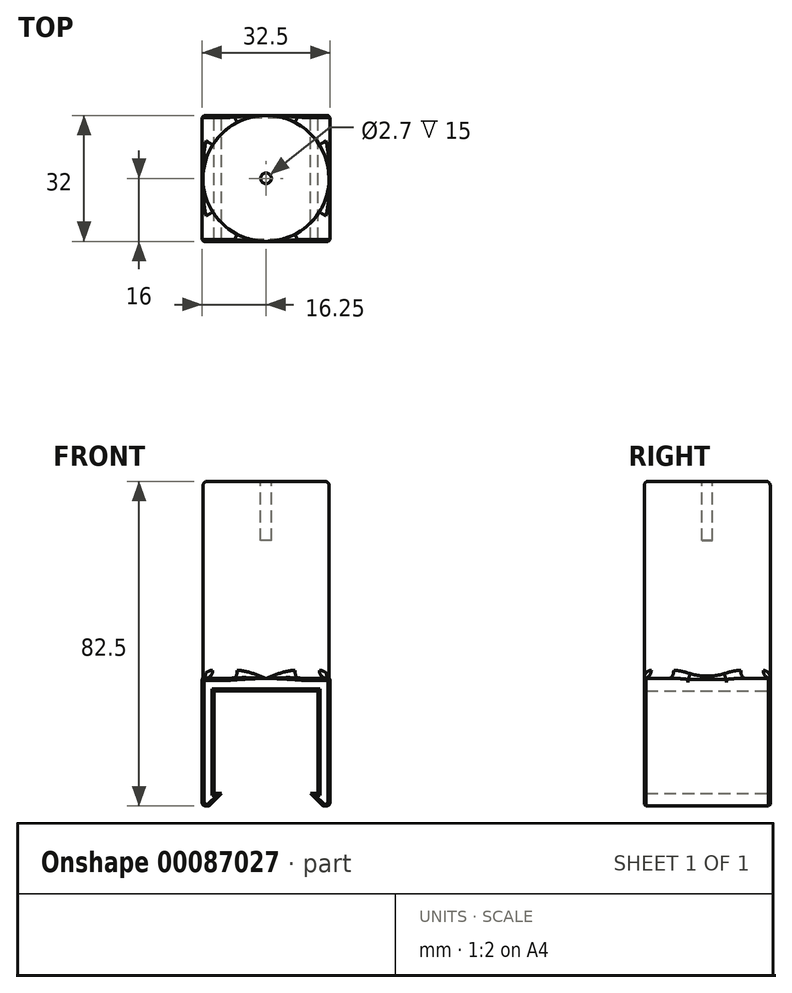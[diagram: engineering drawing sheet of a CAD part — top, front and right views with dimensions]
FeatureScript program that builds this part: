
annotation { "Feature Type Name" : "Feature", "Feature Type Description" : "" }
export const myFeature = defineFeature(function(context is Context, id is Id, definition is map)
    precondition{}
    {
        {
            var Q0;
            Q0=qCreatedBy(makeId("Front.planeOp"),FACE);
            var sketch = newSketch(context, id + "F0", { "sketchPlane" : qUnion([Q0])});
            skLineSegment(sketch, "E0.top", {"start": v(13.25, 13) * mm, "end": v(-13.25, 13) * mm, "construction": true});
            skLineSegment(sketch, "E0.left", {"start": v(13.25, -13) * mm, "end": v(13.25, 13) * mm, "construction": true});
            skLineSegment(sketch, "E0.right", {"start": v(-13.25, -13) * mm, "end": v(-13.25, 13) * mm, "construction": true});
            skPoint(sketch, "E0.middle", {"position": v(0, 0) * mm});
            skLineSegment(sketch, "E1", {"start": v(-13.25, -13) * mm, "end": v(-13.25, 13) * mm});
            skLineSegment(sketch, "E2", {"start": v(13.25, 13) * mm, "end": v(13.25, -13) * mm});
            skLineSegment(sketch, "E3", {"start": v(11.25, -13) * mm, "end": v(14.5, -16.25) * mm});
            skLineSegment(sketch, "E4", {"start": v(14.5, -16.25) * mm, "end": v(16.25, -16.25) * mm});
            skLineSegment(sketch, "E5", {"start": v(16.25, -16.25) * mm, "end": v(16.25, 16.25) * mm});
            skLineSegment(sketch, "E6", {"start": v(16.25, 16.25) * mm, "end": v(-16.25, 16.25) * mm});
            skLineSegment(sketch, "E7", {"start": v(-16.25, 16.25) * mm, "end": v(-16.25, -16.25) * mm});
            skLineSegment(sketch, "E8", {"start": v(-16.25, -16.25) * mm, "end": v(-14.5, -16.25) * mm});
            skLineSegment(sketch, "E9", {"start": v(-14.5, -16.25) * mm, "end": v(-11.25, -13) * mm});
            skLineSegment(sketch, "E10", {"start": v(-11.25, -13) * mm, "end": v(-13.25, -13) * mm});
            skLineSegment(sketch, "E11", {"start": v(-13.25, 13) * mm, "end": v(13.25, 13) * mm});
            skLineSegment(sketch, "E12", {"start": v(11.25, -13) * mm, "end": v(13.25, -13) * mm});
            skSolve(sketch);
        }
        {
            var Q0;
            Q0 = qSketchRegion(id + "F0", true);
            extrude(context, id + "F1", {"entities" : qUnion([Q0]), "endBound" : BoundingType.SYMMETRIC, "depth" : 32 * mm});
        }
        {
            var Q0;
            Q0=makeQuery(id+"F1.opExtrude","SWEPT_FACE",FACE,{"disambiguationData":[OSD([sQuery(id+"F0.wireOp",EDGE,"E6")])]});
            var sketch = newSketch(context, id + "F2", { "sketchPlane" : qUnion([Q0])});
            skCircle(sketch, "E13", {"center": v(0, 0) * mm, "radius": 16 * mm});
            skSolve(sketch);
        }
        {
            var Q0;
            Q0 = qSketchRegion(id + "F2", true);
            extrude(context, id + "F3", {"entities" : qUnion([Q0]), "operationType" : NewBodyOperationType.ADD, "offsetDistance" : 25 * mm, "depth" : 50 * mm});
        }
        {
            var Q0;
            Q0=makeQuery(id+"F3.opExtrude","CAP_FACE",FACE,{"disambiguationData":[OSD([sQuery(id+"F2.wireOp",EDGE,"E13")])],"isStart":false});
            var sketch = newSketch(context, id + "F4", { "sketchPlane" : qUnion([Q0])});
            skCircle(sketch, "E14", {"center": v(0, 0) * mm, "radius": 1.35 * mm});
            skSolve(sketch);
        }
        {
            var Q0;
            Q0 = qSketchRegion(id + "F4", true);
            extrude(context, id + "F5", {"entities" : qUnion([Q0]), "operationType" : NewBodyOperationType.REMOVE, "oppositeDirection" : true, "depth" : 15 * mm});
        }
        {
            var Q0;
            Q0=makeQuery(id+"F1.opExtrude","SWEPT_EDGE",EDGE,{"disambiguationData":[OSD([sQuery(id+"F0.wireOp",EDGE,"E7"),sQuery(id+"F0.wireOp",EDGE,"E8")])]});
            var Q1;
            Q1=makeQuery(id+"F1.opExtrude","SWEPT_EDGE",EDGE,{"disambiguationData":[OSD([sQuery(id+"F0.wireOp",EDGE,"E8"),sQuery(id+"F0.wireOp",EDGE,"E9")])]});
            var Q2;
            Q2=makeQuery(id+"F1.opExtrude","SWEPT_EDGE",EDGE,{"disambiguationData":[OSD([sQuery(id+"F0.wireOp",EDGE,"E3"),sQuery(id+"F0.wireOp",EDGE,"E4")])]});
            var Q3;
            Q3=makeQuery(id+"F1.opExtrude","SWEPT_EDGE",EDGE,{"disambiguationData":[OSD([sQuery(id+"F0.wireOp",EDGE,"E4"),sQuery(id+"F0.wireOp",EDGE,"E5")])]});
            var Q4;
            {var subQ0=sQuery(id+"F0.wireOp",EDGE,"E6");var subQ1=sQuery(id+"F0.wireOp",EDGE,"E5");Q4=makeQuery(id+"F3.boolean.opBoolean","SPLIT",EDGE,{"disambiguationData":[TD([makeQuery(id+"F1.opExtrude","CAP_FACE",FACE,{"disambiguationData":[OSD([sQuery(id+"F0.wireOp",EDGE,"E1"),sQuery(id+"F0.wireOp",EDGE,"E2"),sQuery(id+"F0.wireOp",EDGE,"E3"),sQuery(id+"F0.wireOp",EDGE,"E4"),subQ1,subQ0,sQuery(id+"F0.wireOp",EDGE,"E7"),sQuery(id+"F0.wireOp",EDGE,"E8"),sQuery(id+"F0.wireOp",EDGE,"E9"),sQuery(id+"F0.wireOp",EDGE,"E10"),sQuery(id+"F0.wireOp",EDGE,"E11"),sQuery(id+"F0.wireOp",EDGE,"E12")])],"isStart":false})])],"derivedFrom":makeQuery(id+"F1.opExtrude","SWEPT_EDGE",EDGE,{"disambiguationData":[OSD([subQ1,subQ0])]})});}
            var Q5;
            {var subQ0=sQuery(id+"F0.wireOp",EDGE,"E7");var subQ1=sQuery(id+"F0.wireOp",EDGE,"E6");Q5=makeQuery(id+"F3.boolean.opBoolean","SPLIT",EDGE,{"disambiguationData":[TD([makeQuery(id+"F1.opExtrude","CAP_FACE",FACE,{"disambiguationData":[OSD([sQuery(id+"F0.wireOp",EDGE,"E1"),sQuery(id+"F0.wireOp",EDGE,"E2"),sQuery(id+"F0.wireOp",EDGE,"E3"),sQuery(id+"F0.wireOp",EDGE,"E4"),sQuery(id+"F0.wireOp",EDGE,"E5"),subQ1,subQ0,sQuery(id+"F0.wireOp",EDGE,"E8"),sQuery(id+"F0.wireOp",EDGE,"E9"),sQuery(id+"F0.wireOp",EDGE,"E10"),sQuery(id+"F0.wireOp",EDGE,"E11"),sQuery(id+"F0.wireOp",EDGE,"E12")])],"isStart":false})])],"derivedFrom":makeQuery(id+"F1.opExtrude","SWEPT_EDGE",EDGE,{"disambiguationData":[OSD([subQ1,subQ0])]})});}
            var Q6;
            Q6=makeQuery(id+"F3.opExtrude","CAP_EDGE",EDGE,{"disambiguationData":[OSD([sQuery(id+"F2.wireOp",EDGE,"E13")])],"isStart":false});
            fillet(context, id + "F6", {"entities" : qUnion([Q0, Q1, Q2, Q3, Q4, Q5, Q6]), "radius" : 1 * mm, "tangentPropagation" : true, "allowEdgeOverflow" : false});
        }
        {
            var Q0;
            {var subQ0=sQuery(id+"F2.wireOp",EDGE,"E13");var subQ1=makeQuery(id+"F3.opExtrude","SWEPT_FACE",FACE,{"disambiguationData":[OSD([subQ0])]});var subQ2=sQuery(id+"F0.wireOp",EDGE,"E6");var subQ3=sQuery(id+"F0.wireOp",EDGE,"E5");var subQ4=makeQuery(id+"F1.opExtrude","SWEPT_FACE",FACE,{"disambiguationData":[OSD([subQ2])]});Q0=makeQuery(id+"F3.boolean.opBoolean","SPLIT",EDGE,{"disambiguationData":[topologyDisambiguationEdgeConnected([subQ4,subQ1]),TD([makeQuery(id+"F1.opExtrude","CAP_FACE",FACE,{"disambiguationData":[OSD([sQuery(id+"F0.wireOp",EDGE,"E1"),sQuery(id+"F0.wireOp",EDGE,"E2"),sQuery(id+"F0.wireOp",EDGE,"E3"),sQuery(id+"F0.wireOp",EDGE,"E4"),subQ3,subQ2,sQuery(id+"F0.wireOp",EDGE,"E7"),sQuery(id+"F0.wireOp",EDGE,"E8"),sQuery(id+"F0.wireOp",EDGE,"E9"),sQuery(id+"F0.wireOp",EDGE,"E10"),sQuery(id+"F0.wireOp",EDGE,"E11"),sQuery(id+"F0.wireOp",EDGE,"E12")])],"isStart":true}),makeQuery(id+"F1.opExtrude","SWEPT_FACE",FACE,{"disambiguationData":[OSD([subQ3])]}),subQ4,subQ1,makeQuery(id+"F3.opExtrude","CAP_FACE",FACE,{"disambiguationData":[OSD([subQ0])],"isStart":true})])],"derivedFrom":makeQuery(id+"F3.opExtrude","CAP_EDGE",EDGE,{"disambiguationData":[OSD([subQ0])],"isStart":true})});}
            var Q1;
            {var subQ0=sQuery(id+"F2.wireOp",EDGE,"E13");var subQ1=makeQuery(id+"F3.opExtrude","SWEPT_FACE",FACE,{"disambiguationData":[OSD([subQ0])]});var subQ2=sQuery(id+"F0.wireOp",EDGE,"E7");var subQ3=sQuery(id+"F0.wireOp",EDGE,"E6");var subQ4=makeQuery(id+"F1.opExtrude","SWEPT_FACE",FACE,{"disambiguationData":[OSD([subQ3])]});Q1=makeQuery(id+"F3.boolean.opBoolean","SPLIT",EDGE,{"disambiguationData":[topologyDisambiguationEdgeConnected([subQ4,subQ1]),TD([makeQuery(id+"F1.opExtrude","CAP_FACE",FACE,{"disambiguationData":[OSD([sQuery(id+"F0.wireOp",EDGE,"E1"),sQuery(id+"F0.wireOp",EDGE,"E2"),sQuery(id+"F0.wireOp",EDGE,"E3"),sQuery(id+"F0.wireOp",EDGE,"E4"),sQuery(id+"F0.wireOp",EDGE,"E5"),subQ3,subQ2,sQuery(id+"F0.wireOp",EDGE,"E8"),sQuery(id+"F0.wireOp",EDGE,"E9"),sQuery(id+"F0.wireOp",EDGE,"E10"),sQuery(id+"F0.wireOp",EDGE,"E11"),sQuery(id+"F0.wireOp",EDGE,"E12")])],"isStart":true}),subQ4,makeQuery(id+"F1.opExtrude","SWEPT_FACE",FACE,{"disambiguationData":[OSD([subQ2])]}),subQ1,makeQuery(id+"F3.opExtrude","CAP_FACE",FACE,{"disambiguationData":[OSD([subQ0])],"isStart":true})])],"derivedFrom":makeQuery(id+"F3.opExtrude","CAP_EDGE",EDGE,{"disambiguationData":[OSD([subQ0])],"isStart":true})});}
            var Q2;
            {var subQ0=sQuery(id+"F2.wireOp",EDGE,"E13");var subQ1=makeQuery(id+"F3.opExtrude","SWEPT_FACE",FACE,{"disambiguationData":[OSD([subQ0])]});var subQ2=sQuery(id+"F0.wireOp",EDGE,"E7");var subQ3=sQuery(id+"F0.wireOp",EDGE,"E6");var subQ4=makeQuery(id+"F1.opExtrude","SWEPT_FACE",FACE,{"disambiguationData":[OSD([subQ3])]});Q2=makeQuery(id+"F3.boolean.opBoolean","SPLIT",EDGE,{"disambiguationData":[topologyDisambiguationEdgeConnected([subQ4,subQ1]),TD([makeQuery(id+"F1.opExtrude","CAP_FACE",FACE,{"disambiguationData":[OSD([sQuery(id+"F0.wireOp",EDGE,"E1"),sQuery(id+"F0.wireOp",EDGE,"E2"),sQuery(id+"F0.wireOp",EDGE,"E3"),sQuery(id+"F0.wireOp",EDGE,"E4"),sQuery(id+"F0.wireOp",EDGE,"E5"),subQ3,subQ2,sQuery(id+"F0.wireOp",EDGE,"E8"),sQuery(id+"F0.wireOp",EDGE,"E9"),sQuery(id+"F0.wireOp",EDGE,"E10"),sQuery(id+"F0.wireOp",EDGE,"E11"),sQuery(id+"F0.wireOp",EDGE,"E12")])],"isStart":false}),subQ4,makeQuery(id+"F1.opExtrude","SWEPT_FACE",FACE,{"disambiguationData":[OSD([subQ2])]}),subQ1,makeQuery(id+"F3.opExtrude","CAP_FACE",FACE,{"disambiguationData":[OSD([subQ0])],"isStart":true})])],"derivedFrom":makeQuery(id+"F3.opExtrude","CAP_EDGE",EDGE,{"disambiguationData":[OSD([subQ0])],"isStart":true})});}
            var Q3;
            {var subQ0=sQuery(id+"F2.wireOp",EDGE,"E13");var subQ1=makeQuery(id+"F3.opExtrude","SWEPT_FACE",FACE,{"disambiguationData":[OSD([subQ0])]});var subQ2=sQuery(id+"F0.wireOp",EDGE,"E5");var subQ3=sQuery(id+"F0.wireOp",EDGE,"E6");var subQ4=makeQuery(id+"F1.opExtrude","SWEPT_FACE",FACE,{"disambiguationData":[OSD([subQ3])]});Q3=makeQuery(id+"F3.boolean.opBoolean","SPLIT",EDGE,{"disambiguationData":[topologyDisambiguationEdgeConnected([subQ4,subQ1]),TD([makeQuery(id+"F1.opExtrude","CAP_FACE",FACE,{"disambiguationData":[OSD([sQuery(id+"F0.wireOp",EDGE,"E1"),sQuery(id+"F0.wireOp",EDGE,"E2"),sQuery(id+"F0.wireOp",EDGE,"E3"),sQuery(id+"F0.wireOp",EDGE,"E4"),subQ2,subQ3,sQuery(id+"F0.wireOp",EDGE,"E7"),sQuery(id+"F0.wireOp",EDGE,"E8"),sQuery(id+"F0.wireOp",EDGE,"E9"),sQuery(id+"F0.wireOp",EDGE,"E10"),sQuery(id+"F0.wireOp",EDGE,"E11"),sQuery(id+"F0.wireOp",EDGE,"E12")])],"isStart":false}),makeQuery(id+"F1.opExtrude","SWEPT_FACE",FACE,{"disambiguationData":[OSD([subQ2])]}),subQ4,subQ1,makeQuery(id+"F3.opExtrude","CAP_FACE",FACE,{"disambiguationData":[OSD([subQ0])],"isStart":true})])],"derivedFrom":makeQuery(id+"F3.opExtrude","CAP_EDGE",EDGE,{"disambiguationData":[OSD([subQ0])],"isStart":true})});}
            fillet(context, id + "F7", {"entities" : qUnion([Q0, Q1, Q2, Q3]), "radius" : 2 * mm, "tangentPropagation" : true, "defaultsChanged" : false, "vertexSettings" : [], "allowEdgeOverflow" : false});
        }
        {
            var Q0;
            Q0=makeQuery(id+"F1.opExtrude","CAP_EDGE",EDGE,{"disambiguationData":[OSD([sQuery(id+"F0.wireOp",EDGE,"E5")])],"isStart":false});
            var Q1;
            Q1=makeQuery(id+"F1.opExtrude","CAP_EDGE",EDGE,{"disambiguationData":[OSD([sQuery(id+"F0.wireOp",EDGE,"E7")])],"isStart":false});
            var Q2;
            Q2=makeQuery(id+"F1.opExtrude","CAP_EDGE",EDGE,{"disambiguationData":[OSD([sQuery(id+"F0.wireOp",EDGE,"E1")])],"isStart":false});
            var Q3;
            Q3=makeQuery(id+"F1.opExtrude","CAP_EDGE",EDGE,{"disambiguationData":[OSD([sQuery(id+"F0.wireOp",EDGE,"E11")])],"isStart":false});
            var Q4;
            Q4=makeQuery(id+"F1.opExtrude","CAP_EDGE",EDGE,{"disambiguationData":[OSD([sQuery(id+"F0.wireOp",EDGE,"E2")])],"isStart":false});
            var Q5;
            Q5=makeQuery(id+"F1.opExtrude","CAP_EDGE",EDGE,{"disambiguationData":[OSD([sQuery(id+"F0.wireOp",EDGE,"E5")])],"isStart":true});
            var Q6;
            Q6=makeQuery(id+"F1.opExtrude","CAP_EDGE",EDGE,{"disambiguationData":[OSD([sQuery(id+"F0.wireOp",EDGE,"E7")])],"isStart":true});
            var Q7;
            Q7=makeQuery(id+"F1.opExtrude","CAP_EDGE",EDGE,{"disambiguationData":[OSD([sQuery(id+"F0.wireOp",EDGE,"E1")])],"isStart":true});
            var Q8;
            Q8=makeQuery(id+"F1.opExtrude","CAP_EDGE",EDGE,{"disambiguationData":[OSD([sQuery(id+"F0.wireOp",EDGE,"E11")])],"isStart":true});
            var Q9;
            Q9=makeQuery(id+"F1.opExtrude","CAP_EDGE",EDGE,{"disambiguationData":[OSD([sQuery(id+"F0.wireOp",EDGE,"E2")])],"isStart":true});
            var Q10;
            Q10=makeQuery(id+"F1.opExtrude","CAP_EDGE",EDGE,{"disambiguationData":[OSD([sQuery(id+"F0.wireOp",EDGE,"E12")])],"isStart":true});
            var Q11;
            Q11=makeQuery(id+"F1.opExtrude","CAP_EDGE",EDGE,{"disambiguationData":[OSD([sQuery(id+"F0.wireOp",EDGE,"E10")])],"isStart":true});
            var Q12;
            Q12=makeQuery(id+"F1.opExtrude","CAP_EDGE",EDGE,{"disambiguationData":[OSD([sQuery(id+"F0.wireOp",EDGE,"E10")])],"isStart":false});
            var Q13;
            Q13=makeQuery(id+"F1.opExtrude","CAP_EDGE",EDGE,{"disambiguationData":[OSD([sQuery(id+"F0.wireOp",EDGE,"E12")])],"isStart":false});
            chamfer(context, id + "F8", {"entities" : qUnion([Q0, Q1, Q2, Q3, Q4, Q5, Q6, Q7, Q8, Q9, Q10, Q11, Q12, Q13]), "width" : 0.5 * mm, "tangentPropagation" : true});
        }
    });
